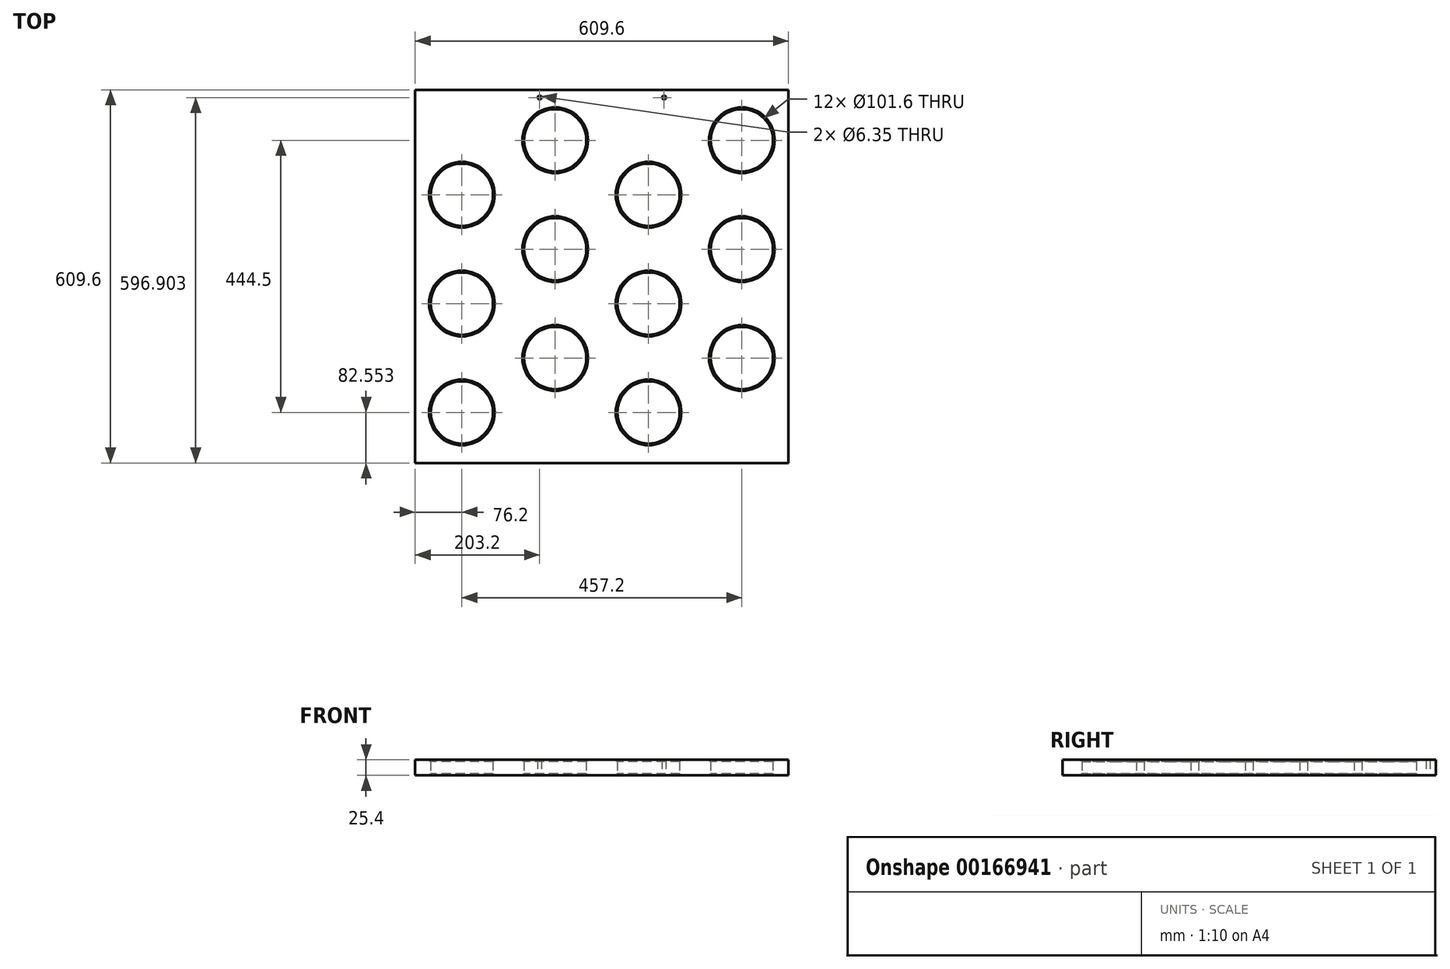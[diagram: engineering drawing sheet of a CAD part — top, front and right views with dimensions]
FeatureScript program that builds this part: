
annotation { "Feature Type Name" : "Feature", "Feature Type Description" : "" }
export const myFeature = defineFeature(function(context is Context, id is Id, definition is map)
    precondition{}
    {
        {
            var Q0;
            Q0=qCreatedBy(makeId("Top.planeOp"),FACE);
            var sketch = newSketch(context, id + "F0", { "sketchPlane" : qUnion([Q0])});
            skLineSegment(sketch, "E0.bottom", {"start": v(304.8, 274.05) * mm, "end": v(-304.8, 274.05) * mm});
            skLineSegment(sketch, "E0.top", {"start": v(304.8, -335.55) * mm, "end": v(-304.8, -335.55) * mm});
            skLineSegment(sketch, "E0.left", {"start": v(304.8, 274.05) * mm, "end": v(304.8, -335.55) * mm});
            skLineSegment(sketch, "E0.right", {"start": v(-304.8, 274.05) * mm, "end": v(-304.8, -335.55) * mm});
            skPoint(sketch, "E0.middle", {"position": v(0, -30.75) * mm});
            skCircle(sketch, "E1", {"center": v(-76.2, 191.5) * mm, "radius": 50.8 * mm});
            skCircle(sketch, "E2", {"center": v(-228.6, 102.6) * mm, "radius": 50.8 * mm});
            skCircle(sketch, "E3", {"center": v(-76.2, 13.7) * mm, "radius": 50.8 * mm});
            skCircle(sketch, "E4", {"center": v(-228.6, -75.2) * mm, "radius": 50.8 * mm});
            skCircle(sketch, "E5", {"center": v(228.6, 191.5) * mm, "radius": 50.8 * mm});
            skCircle(sketch, "E6", {"center": v(76.2, 102.6) * mm, "radius": 50.8 * mm});
            skCircle(sketch, "E7", {"center": v(228.6, 13.7) * mm, "radius": 50.8 * mm});
            skCircle(sketch, "E8", {"center": v(76.2, -75.2) * mm, "radius": 50.8 * mm});
            skCircle(sketch, "E9", {"center": v(-76.2, -164.1) * mm, "radius": 50.8 * mm});
            skCircle(sketch, "E10", {"center": v(-228.6, -253) * mm, "radius": 50.8 * mm});
            skCircle(sketch, "E11", {"center": v(228.6, -164.1) * mm, "radius": 50.8 * mm});
            skCircle(sketch, "E12", {"center": v(76.2, -253) * mm, "radius": 50.8 * mm});
            skCircle(sketch, "E13", {"center": v(-101.6, 261.35) * mm, "radius": 3.18 * mm});
            skCircle(sketch, "E14", {"center": v(101.6, 261.35) * mm, "radius": 3.18 * mm});
            skSolve(sketch);
        }
        {
            var Q0;
            Q0 = qSketchRegion(id + "F0", true);
            extrude(context, id + "F1", {"entities" : qUnion([Q0]), "depth" : 25.4 * mm});
        }
        {
            var Q0;
            Q0=makeQuery(id+"F1.opExtrude","SWEPT_FACE",FACE,{"disambiguationData":[OSD([sQuery(id+"F0.wireOp",EDGE,"E9")])]});
            var Q1;
            Q1=makeQuery(id+"F1.opExtrude","SWEPT_FACE",FACE,{"disambiguationData":[OSD([sQuery(id+"F0.wireOp",EDGE,"E3")])]});
            var Q2;
            Q2=makeQuery(id+"F1.opExtrude","SWEPT_FACE",FACE,{"disambiguationData":[OSD([sQuery(id+"F0.wireOp",EDGE,"E2")])]});
            var Q3;
            Q3=makeQuery(id+"F1.opExtrude","SWEPT_FACE",FACE,{"disambiguationData":[OSD([sQuery(id+"F0.wireOp",EDGE,"E1")])]});
            var Q4;
            Q4=makeQuery(id+"F1.opExtrude","SWEPT_FACE",FACE,{"disambiguationData":[OSD([sQuery(id+"F0.wireOp",EDGE,"E6")])]});
            var Q5;
            Q5=makeQuery(id+"F1.opExtrude","SWEPT_FACE",FACE,{"disambiguationData":[OSD([sQuery(id+"F0.wireOp",EDGE,"E5")])]});
            var Q6;
            Q6=makeQuery(id+"F1.opExtrude","SWEPT_FACE",FACE,{"disambiguationData":[OSD([sQuery(id+"F0.wireOp",EDGE,"E7")])]});
            var Q7;
            Q7=makeQuery(id+"F1.opExtrude","SWEPT_FACE",FACE,{"disambiguationData":[OSD([sQuery(id+"F0.wireOp",EDGE,"E8")])]});
            var Q8;
            Q8=makeQuery(id+"F1.opExtrude","SWEPT_FACE",FACE,{"disambiguationData":[OSD([sQuery(id+"F0.wireOp",EDGE,"E4")])]});
            var Q9;
            Q9=makeQuery(id+"F1.opExtrude","SWEPT_FACE",FACE,{"disambiguationData":[OSD([sQuery(id+"F0.wireOp",EDGE,"E10")])]});
            var Q10;
            Q10=makeQuery(id+"F1.opExtrude","SWEPT_FACE",FACE,{"disambiguationData":[OSD([sQuery(id+"F0.wireOp",EDGE,"E12")])]});
            var Q11;
            Q11=makeQuery(id+"F1.opExtrude","SWEPT_FACE",FACE,{"disambiguationData":[OSD([sQuery(id+"F0.wireOp",EDGE,"E11")])]});
            chamfer(context, id + "F2", {"entities" : qUnion([Q0, Q1, Q2, Q3, Q4, Q5, Q6, Q7, Q8, Q9, Q10, Q11]), "width" : 2.86 * mm, "tangentPropagation" : true});
        }
    });
